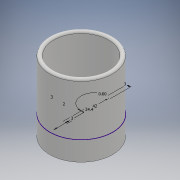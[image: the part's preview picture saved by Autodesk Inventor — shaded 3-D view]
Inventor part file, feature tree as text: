
AUTODESK INVENTOR PART (.ipt)
format: ipt  version: 2018 (Build 220112000, 112)  size: 239,104 bytes
history: native  units: mm
features: fillet x6, extrude x3, sketch x1
ambient origin geometry x8: Origin, YZ Plane, XZ Plane, XY Plane, X Axis, Y Axis, Z Axis, Center Point
bodies: Solid1 (feature_tree)
feature tree (10):
  sketch  "Sketch1"  dims[d0=24.4mm d1=42.0mm d2=3.0mm d3=2.0mm d4=3.0mm d6=3.0mm d7=180.0deg d8=10.0mm d9=0.0mm d10=15.0mm d11=0.0mm d13=40.0mm d14=0.0mm d16=2.0mm d17=1.0mm d18=1.0mm d19=1.0mm d24=1.5mm d25=1.5mm]
  extrude  "Extrusion1"  Depth=1.5mm
  extrude  "Extrusion2"  Depth=1.5mm
  extrude  "Extrusion3"  Depth=1.5mm
  fillet  "Fillet3"  Radius=3.0mm
  fillet  "Fillet4"  Radius=3.0mm
  fillet  "Fillet5"  [1 undecoded]
  fillet  "Fillet6"  Radius=10.0mm
  fillet  "Fillet8"  Radius=15.0mm
  fillet  "Fillet9"  Radius=40.0mm
note: 1 required parameter value undecoded (feature->parameter linkage not recoverable at this tier; creation-order binding heuristic only, values carry confidence <= 0.55)
